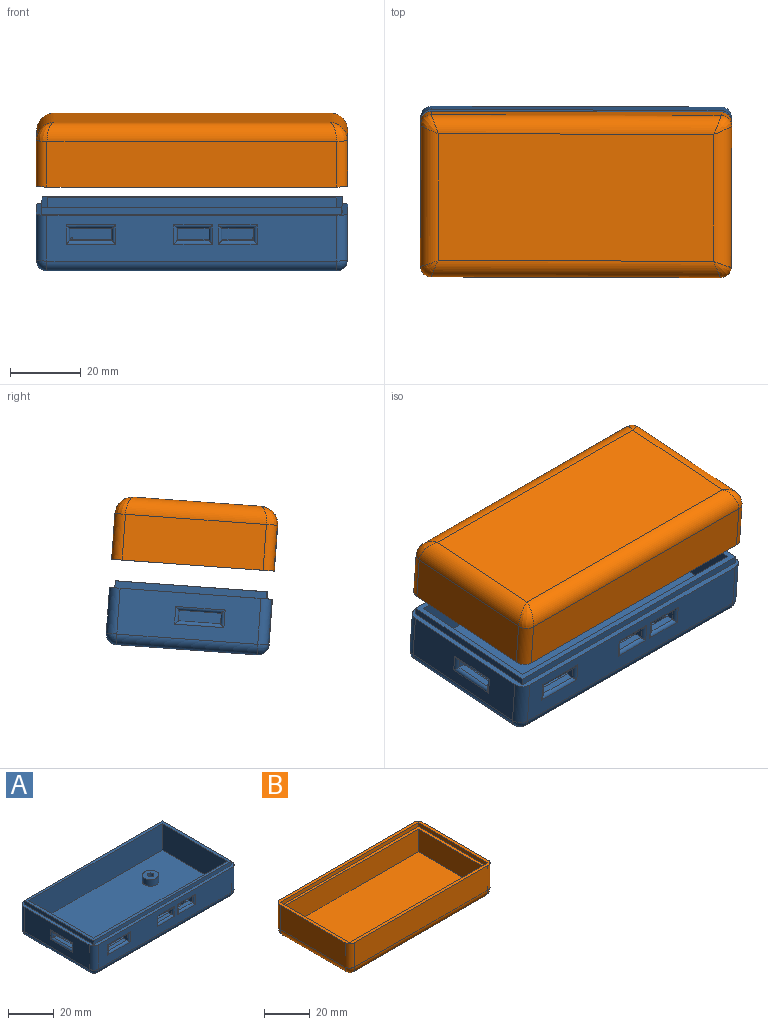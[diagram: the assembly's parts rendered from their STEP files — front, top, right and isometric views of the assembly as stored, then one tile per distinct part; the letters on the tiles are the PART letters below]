
ASSEMBLY  parts=2 mates=1
PART A: 76 faces, bbox 88x46x18 mm
  f0: plane 88x46mm, normal (0,0,1), area 385.3mm2, adj f2,f3,f4,f5,f6,f7,f8,f9
  f1: plane 82x40mm, normal (0,0,-1), area 3280mm2, adj f21,f22,f25,f26
  f2: plane 40x13mm, normal (-1,0,0), area 450mm2, adj f0,f18,f19,f22,f72,f73,f74,f75
  f3: plane 82x13mm, normal (0,-1,0), area 869mm2, adj f0,f16,f19,f26,f60,f61,f62,f63
  f4: plane 40x13mm, normal (1,0,0), area 520mm2, adj f0,f16,f17,f25
  f5: plane 82x13mm, normal (0,1,0), area 1066mm2, adj f0,f17,f18,f21
  f6: plane 43x2mm, normal (-1,0,0), area 86mm2, adj f0,f7,f9,f10
  f7: plane 85x2mm, normal (0,-1,0), area 170mm2, adj f0,f6,f8,f10
  f8: plane 43x2mm, normal (1,0,0), area 86mm2, adj f0,f7,f9,f10
  f9: plane 85x2mm, normal (0,1,0), area 170mm2, adj f0,f6,f8,f10
  f10: plane 85x43mm, normal (0,0,1), area 375mm2, adj f6,f7,f8,f9,f12,f13,f14,f15
  f11: plane 82x40mm, normal (0,0,1), area 3123.8mm2, adj f12,f13,f14,f15,f29,f33,f37,f41
  f12: plane 40x14mm, normal (1,0,0), area 524mm2, adj f10,f11,f13,f15,f44,f45,f46,f47
  f13: plane 82x14mm, normal (0,1,0), area 1043.8mm2, adj f10,f11,f12,f14,f48,f49,f50,f51
  f14: plane 40x14mm, normal (-1,0,0), area 560mm2, adj f10,f11,f13,f15
  f15: plane 82x14mm, normal (0,-1,0), area 1148mm2, adj f10,f11,f12,f14
  f16: cylinder r=3mm len=13mm, axis (0,0,1), area 61.3mm2, adj f0,f3,f4,f27
  f17: cylinder r=3mm len=13mm, axis (0,0,-1), area 61.3mm2, adj f0,f4,f5,f23
  f18: cylinder r=3mm len=13mm, axis (0,0,1), area 61.3mm2, adj f0,f2,f5,f20
  f19: cylinder r=3mm len=13mm, axis (0,0,-1), area 61.3mm2, adj f0,f2,f3,f24
  f20: sphere r=3mm, area 14.1mm2, adj f18,f21,f22
  f21: cylinder r=3mm len=82mm, axis (-1,0,0), area 386.4mm2, adj f1,f5,f20,f23
  f22: cylinder r=3mm len=40mm, axis (0,-1,0), area 188.5mm2, adj f1,f2,f20,f24
  f23: sphere r=3mm, area 14.1mm2, adj f17,f21,f25
  f24: sphere r=3mm, area 14.1mm2, adj f19,f22,f26
  f25: cylinder r=3mm len=40mm, axis (0,1,0), area 188.5mm2, adj f1,f4,f23,f27
  f26: cylinder r=3mm len=82mm, axis (1,0,0), area 386.4mm2, adj f1,f3,f24,f27
  f27: sphere r=3mm, area 14.1mm2, adj f16,f25,f26
  f28: cylinder r=1.45mm len=3.5mm, axis (0,0,-1), area 31.9mm2, adj f30,f31
  f29: cylinder r=3.45mm len=6.9mm, axis (0,0,-1), area 75.9mm2, adj f11,f30
  f30: plane 6.9x6.9mm, normal (0,0,1), area 30.8mm2, adj f28,f29
  f31: plane 2.9x2.9mm, normal (0,0,1), area 6.6mm2, adj f28
  f32: cylinder r=1.45mm len=3.5mm, axis (0,0,-1), area 31.9mm2, adj f34,f35
  f33: cylinder r=3.55mm len=7.1mm, axis (0,0,-1), area 78.1mm2, adj f11,f34
  f34: plane 7.1x7.1mm, normal (0,0,1), area 33mm2, adj f32,f33
  f35: plane 2.9x2.9mm, normal (0,0,1), area 6.6mm2, adj f32
  f36: cylinder r=1.45mm len=3.5mm, axis (0,0,-1), area 31.9mm2, adj f38,f39
  f37: cylinder r=3.55mm len=7.1mm, axis (0,0,-1), area 78.1mm2, adj f11,f38
  f38: plane 7.1x7.1mm, normal (0,0,1), area 33mm2, adj f36,f37
  f39: plane 2.9x2.9mm, normal (0,0,1), area 6.6mm2, adj f36
  f40: cylinder r=1.45mm len=3.5mm, axis (0,0,-1), area 31.9mm2, adj f42,f43
  f41: cylinder r=3.55mm len=7.1mm, axis (0,0,-1), area 78.1mm2, adj f11,f42
  f42: plane 7.1x7.1mm, normal (0,0,1), area 33mm2, adj f40,f41
  f43: plane 2.9x2.9mm, normal (0,0,1), area 6.6mm2, adj f40
  f44: plane 12x2mm, normal (0,0,-1), area 24mm2, adj f12,f45,f46,f74
  f45: plane 3x2mm, normal (0,1,0), area 6mm2, adj f12,f44,f47,f72
  f46: plane 3x2mm, normal (0,-1,0), area 6mm2, adj f12,f44,f47,f75
  f47: plane 12x2mm, normal (0,0,1), area 24mm2, adj f12,f45,f46,f73
  f48: plane 9x2mm, normal (0,0,-1), area 18mm2, adj f13,f49,f50,f63
  f49: plane 3.47x2mm, normal (-1,0,0), area 6.9mm2, adj f13,f48,f51,f61
  f50: plane 3.47x2mm, normal (1,0,0), area 6.9mm2, adj f13,f48,f51,f62
  f51: plane 9x2mm, normal (0,0,1), area 18mm2, adj f13,f49,f50,f60
  f52: plane 9x2mm, normal (0,0,-1), area 18mm2, adj f13,f53,f54,f66
  f53: plane 3.47x2mm, normal (-1,0,0), area 6.9mm2, adj f13,f52,f55,f64
  f54: plane 3.47x2mm, normal (1,0,0), area 6.9mm2, adj f13,f52,f55,f67
  f55: plane 9x2mm, normal (0,0,1), area 18mm2, adj f13,f53,f54,f65
  f56: plane 12x2mm, normal (0,0,-1), area 24mm2, adj f13,f57,f58,f71
  f57: plane 3.47x2mm, normal (-1,0,0), area 6.9mm2, adj f13,f56,f59,f69
  f58: plane 3.47x2mm, normal (1,0,0), area 6.9mm2, adj f13,f56,f59,f70
  f59: plane 12x2mm, normal (0,0,1), area 24mm2, adj f13,f57,f58,f68
  f60: cylinder r=1mm len=11mm, axis (-1,0,0), area 15.3mm2, adj f3,f51,f61,f62
  f61: cylinder r=1mm len=5.47mm, axis (0,0,-1), area 6.6mm2, adj f3,f49,f60,f63
  f62: cylinder r=1mm len=5.47mm, axis (0,0,1), area 6.6mm2, adj f3,f50,f60,f63
  f63: cylinder r=1mm len=11mm, axis (1,0,0), area 15.3mm2, adj f3,f48,f61,f62
  f64: cylinder r=1mm len=5.47mm, axis (0,0,-1), area 6.6mm2, adj f3,f53,f65,f66
  f65: cylinder r=1mm len=11mm, axis (-1,0,0), area 15.3mm2, adj f3,f55,f64,f67
  f66: cylinder r=1mm len=11mm, axis (1,0,0), area 15.3mm2, adj f3,f52,f64,f67
  f67: cylinder r=1mm len=5.47mm, axis (0,0,1), area 6.6mm2, adj f3,f54,f65,f66
  f68: cylinder r=1mm len=14mm, axis (-1,0,0), area 20mm2, adj f3,f59,f69,f70
  f69: cylinder r=1mm len=5.47mm, axis (0,0,-1), area 6.6mm2, adj f3,f57,f68,f71
  f70: cylinder r=1mm len=5.47mm, axis (0,0,1), area 6.6mm2, adj f3,f58,f68,f71
  f71: cylinder r=1mm len=14mm, axis (1,0,0), area 20mm2, adj f3,f56,f69,f70
  f72: cylinder r=1mm len=5mm, axis (0,0,-1), area 5.9mm2, adj f2,f45,f73,f74
  f73: cylinder r=1mm len=14mm, axis (0,1,0), area 20mm2, adj f2,f47,f72,f75
  f74: cylinder r=1mm len=14mm, axis (0,-1,0), area 20mm2, adj f2,f44,f72,f75
  f75: cylinder r=1mm len=5mm, axis (0,0,1), area 5.9mm2, adj f2,f46,f73,f74
PART B: 28 faces, bbox 88x46x18 mm
  f0: plane 40x12mm, normal (-1,0,0), area 480mm2, adj f1,f3,f4,f5
  f1: plane 82x12mm, normal (0,-1,0), area 984mm2, adj f0,f2,f4,f5
  f2: plane 40x12mm, normal (1,0,0), area 480mm2, adj f1,f3,f4,f5
  f3: plane 82x12mm, normal (0,1,0), area 984mm2, adj f0,f2,f4,f5
  f4: plane 85x43mm, normal (0,0,1), area 375mm2, adj f0,f1,f2,f3,f6,f7,f8,f9
  f5: plane 82x40mm, normal (0,0,1), area 3280mm2, adj f0,f1,f2,f3
  f6: plane 85x2mm, normal (0,1,0), area 170mm2, adj f4,f7,f9,f10
  f7: plane 43x2mm, normal (1,0,0), area 86mm2, adj f4,f6,f8,f10
  f8: plane 85x2mm, normal (0,-1,0), area 170mm2, adj f4,f7,f9,f10
  f9: plane 43x2mm, normal (-1,0,0), area 86mm2, adj f4,f6,f8,f10
  f10: plane 88x46mm, normal (0,0,1), area 385.3mm2, adj f6,f7,f8,f9,f12,f13,f14,f15
  f11: plane 78x36mm, normal (0,0,-1), area 2808mm2, adj f21,f22,f25,f26
  f12: plane 82x13mm, normal (0,1,0), area 1066mm2, adj f10,f18,f19,f22
  f13: plane 40x13mm, normal (1,0,0), area 520mm2, adj f10,f17,f18,f21
  f14: plane 82x13mm, normal (0,-1,0), area 1066mm2, adj f10,f16,f17,f25
  f15: plane 40x13mm, normal (-1,0,0), area 520mm2, adj f10,f16,f19,f26
  f16: cylinder r=3mm len=13mm, axis (0,0,-1), area 61.3mm2, adj f10,f14,f15,f27
  f17: cylinder r=3mm len=13mm, axis (0,0,1), area 61.3mm2, adj f10,f13,f14,f23
  f18: cylinder r=3mm len=13mm, axis (0,0,-1), area 61.3mm2, adj f10,f12,f13,f20
  f19: cylinder r=3mm len=13mm, axis (0,0,1), area 61.3mm2, adj f10,f12,f15,f24
  f20: bspline ~6.03x5mm, area 24.5mm2, adj f18,f21,f22
  f21: cylinder r=5mm len=40mm, axis (0,1,0), area 302.7mm2, adj f11,f13,f20,f23
  f22: cylinder r=5mm len=82mm, axis (-1,0,0), area 632.6mm2, adj f11,f12,f20,f24
  f23: bspline ~6.03x5mm, area 24.5mm2, adj f17,f21,f25
  f24: bspline ~6.03x5mm, area 24.5mm2, adj f19,f22,f26
  f25: cylinder r=5mm len=82mm, axis (1,0,0), area 632.6mm2, adj f11,f14,f23,f27
  f26: cylinder r=5mm len=40mm, axis (0,-1,0), area 302.7mm2, adj f11,f15,f24,f27
  f27: bspline ~6.03x5mm, area 24.5mm2, adj f16,f25,f26
PLACE A rot(axis=(1,0,-0.04),4.1deg) t=(-189.63,24.25,108.76)mm
PLACE B rot(axis=(-1,0,0),175.9deg) t=(-189.64,21.22,150.65)mm
MATE slider A.f19 <-> B.f19  axis (0,0.07,-1) through (-230.69,3.11,125.27)mm
